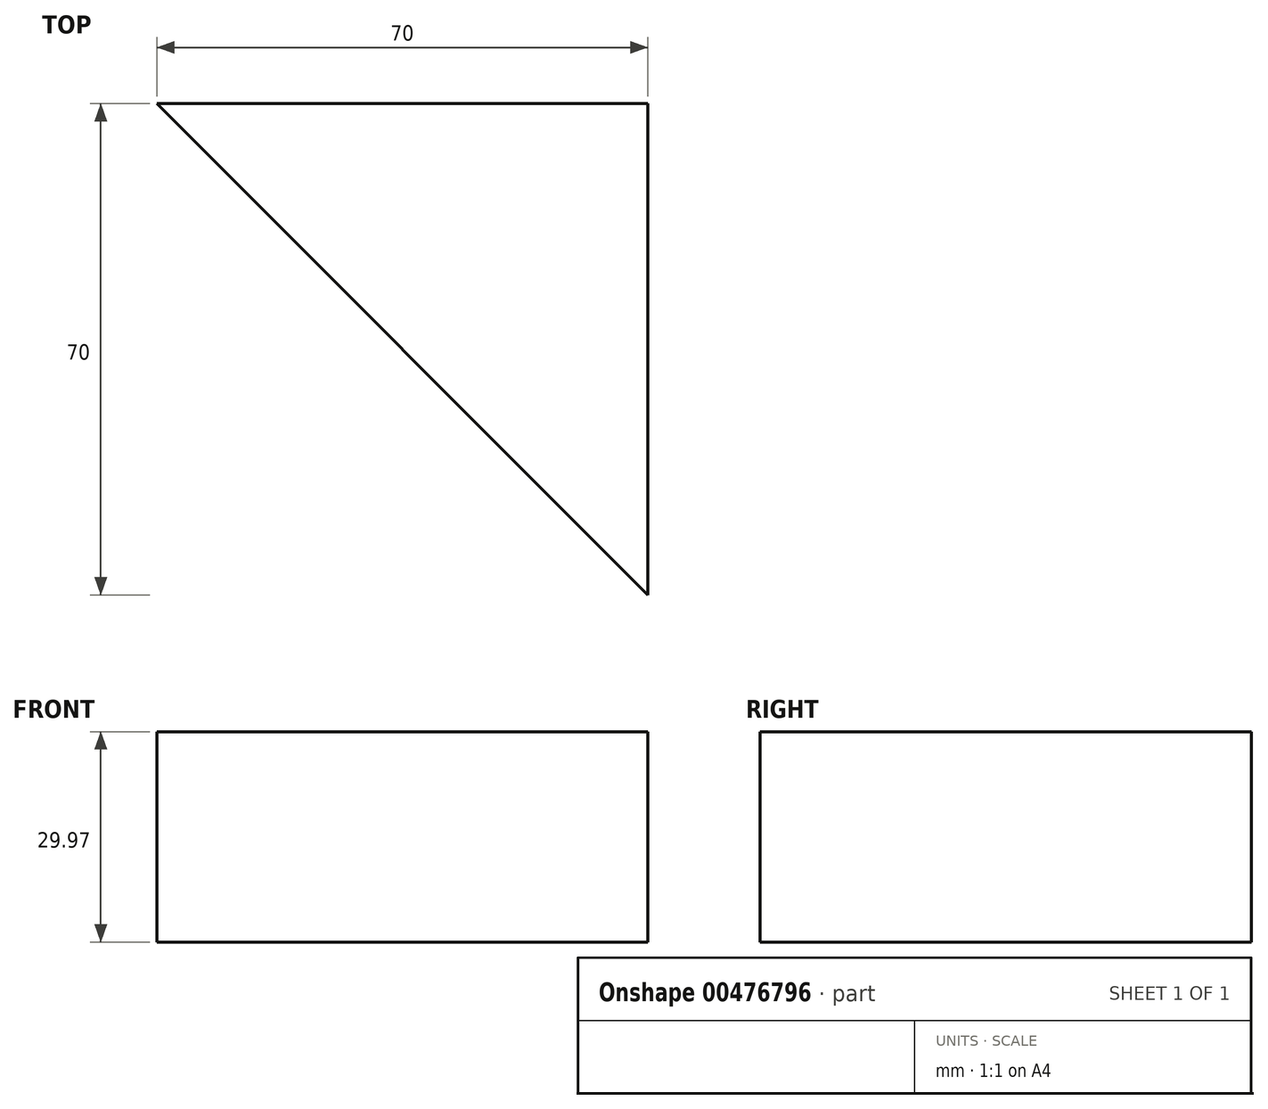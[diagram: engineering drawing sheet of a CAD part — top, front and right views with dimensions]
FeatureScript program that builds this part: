
annotation { "Feature Type Name" : "Feature", "Feature Type Description" : "" }
export const myFeature = defineFeature(function(context is Context, id is Id, definition is map)
    precondition{}
    {
        {
            var Q0;
            Q0=qCreatedBy(makeId("Top.planeOp"),FACE);
            var sketch = newSketch(context, id + "F0", { "sketchPlane" : qUnion([Q0])});
            skLineSegment(sketch, "E0", {"start": v(0, 0) * mm, "end": v(70, 0) * mm});
            skLineSegment(sketch, "E1", {"start": v(70, 0) * mm, "end": v(70, -70) * mm});
            skLineSegment(sketch, "E2", {"start": v(70, -70) * mm, "end": v(0, 0) * mm});
            skSolve(sketch);
        }
        {
            var Q0;
            Q0=makeQuery(id+"F0.imprint","IMPRINT",FACE,{"disambiguationData":[TD([[makeQuery(id+"F0.imprint","IMPRINT",EDGE,{"derivedFrom":sQuery(id+"F0.wireOp",EDGE,"E0")}),-1.0]])]});
            extrude(context, id + "F1", {"entities" : qUnion([Q0]), "depth" : 29.97 * mm});
        }
    });
